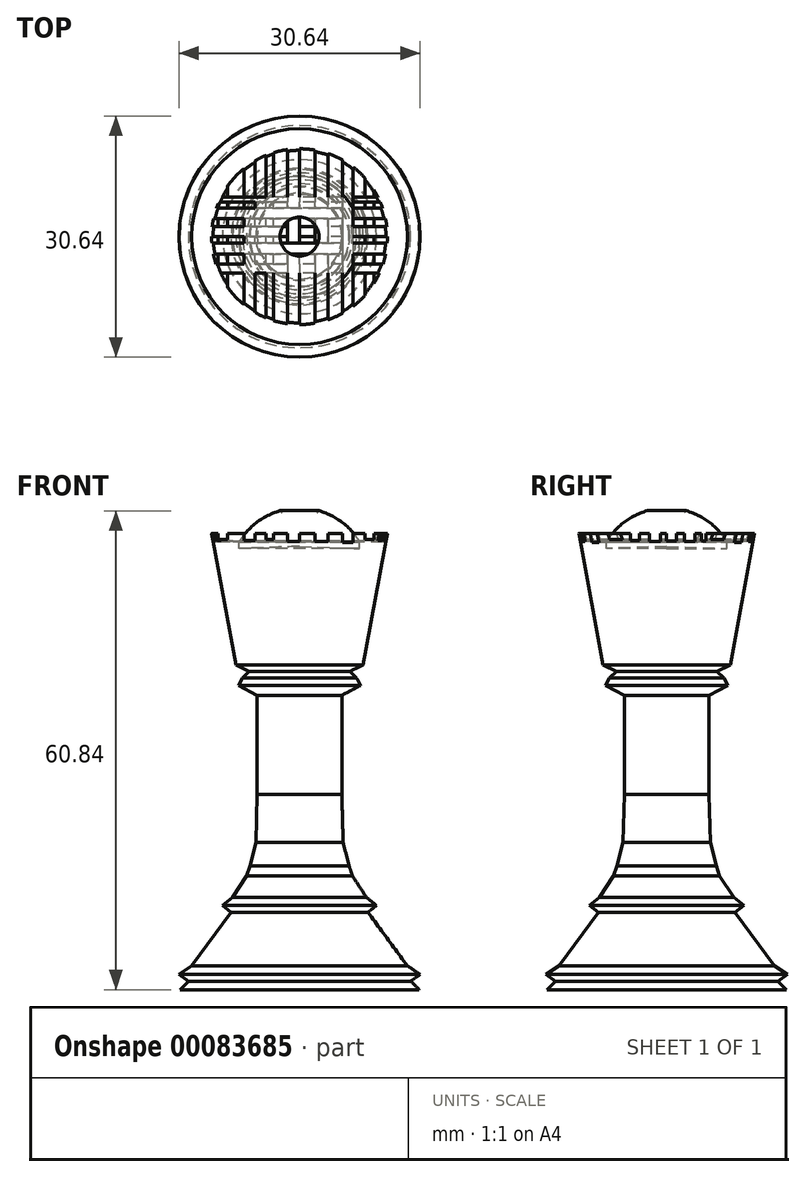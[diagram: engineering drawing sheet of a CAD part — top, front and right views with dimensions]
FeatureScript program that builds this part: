
annotation { "Feature Type Name" : "Feature", "Feature Type Description" : "" }
export const myFeature = defineFeature(function(context is Context, id is Id, definition is map)
    precondition{}
    {
        {
            var Q0;
            Q0=qCreatedBy(makeId("Front.planeOp"),FACE);
            var sketch = newSketch(context, id + "F0", { "sketchPlane" : qUnion([Q0])});
            skLineSegment(sketch, "E0", {"start": v(0, -41.24) * mm, "end": v(15.2, -41.24) * mm});
            skLineSegment(sketch, "E1", {"start": v(15.2, -41.24) * mm, "end": v(14.13, -40.16) * mm});
            skLineSegment(sketch, "E2", {"start": v(14.13, -40.16) * mm, "end": v(15.32, -39.3) * mm});
            skLineSegment(sketch, "E3", {"start": v(15.32, -39.3) * mm, "end": v(13.7, -38.2) * mm});
            skLineSegment(sketch, "E4", {"start": v(13.7, -38.2) * mm, "end": v(8.69, -31.4) * mm});
            skLineSegment(sketch, "E5", {"start": v(8.69, -31.4) * mm, "end": v(9.8, -30.55) * mm});
            skLineSegment(sketch, "E6", {"start": v(9.8, -30.55) * mm, "end": v(8.52, -29.53) * mm});
            skLineSegment(sketch, "E7", {"start": v(8.52, -29.53) * mm, "end": v(6.73, -26.81) * mm});
            skLineSegment(sketch, "E8", {"start": v(6.73, -26.81) * mm, "end": v(6.3, -25.54) * mm});
            skLineSegment(sketch, "E9", {"start": v(6.3, -25.54) * mm, "end": v(5.54, -22.56) * mm});
            skLineSegment(sketch, "E10", {"start": v(5.54, -22.56) * mm, "end": v(5.37, -16.44) * mm});
            skLineSegment(sketch, "E11", {"start": v(5.37, -16.44) * mm, "end": v(5.37, -3.86) * mm});
            skLineSegment(sketch, "E12", {"start": v(5.37, -3.86) * mm, "end": v(7.75, -2.58) * mm});
            skLineSegment(sketch, "E13", {"start": v(7.75, -2.58) * mm, "end": v(7.24, -1.64) * mm});
            skLineSegment(sketch, "E14", {"start": v(7.24, -1.64) * mm, "end": v(6.4, -0.8) * mm});
            skLineSegment(sketch, "E15", {"start": v(6.4, -0.8) * mm, "end": v(8.1, 0) * mm});
            skLineSegment(sketch, "E16", {"start": v(8.1, 0) * mm, "end": v(11.16, 16.74) * mm});
            skLineSegment(sketch, "E17", {"start": v(11.16, 16.74) * mm, "end": v(0, 16.74) * mm});
            skLineSegment(sketch, "E18", {"start": v(0, 16.74) * mm, "end": v(0, -41.24) * mm});
            skSolve(sketch);
        }
        {
            var Q0;
            Q0=makeQuery(id+"F0.imprint","IMPRINT",FACE,{"disambiguationData":[TD([[makeQuery(id+"F0.imprint","IMPRINT",EDGE,{"derivedFrom":sQuery(id+"F0.wireOp",EDGE,"E0")}),1.0]])]});
            var Q1;
            Q1=sQuery(id+"F0.wireOp",EDGE,"E18");
            revolve(context, id + "F1", {"entities" : qUnion([Q0]), "axis" : qUnion([Q1]), "revolveType" : RevolveType.FULL});
        }
        {
            var Q0;
            Q0=qCreatedBy(makeId("Front.planeOp"),FACE);
            var sketch = newSketch(context, id + "F2", { "sketchPlane" : qUnion([Q0])});
            skLineSegment(sketch, "E19.bottom", {"start": v(-1.55, 16.99) * mm, "end": v(0, 16.99) * mm});
            skLineSegment(sketch, "E19.top", {"start": v(-1.55, 15.7) * mm, "end": v(0, 15.7) * mm});
            skLineSegment(sketch, "E19.left", {"start": v(-1.55, 16.99) * mm, "end": v(-1.55, 15.7) * mm});
            skLineSegment(sketch, "E19.right", {"start": v(0, 16.99) * mm, "end": v(0, 15.7) * mm});
            skLineSegment(sketch, "E20.bottom", {"start": v(1.97, 16.87) * mm, "end": v(3.61, 16.87) * mm});
            skLineSegment(sketch, "E20.top", {"start": v(1.97, 15.7) * mm, "end": v(3.61, 15.7) * mm});
            skLineSegment(sketch, "E20.left", {"start": v(1.97, 16.87) * mm, "end": v(1.97, 15.7) * mm});
            skLineSegment(sketch, "E20.right", {"start": v(3.61, 16.87) * mm, "end": v(3.61, 15.7) * mm});
            skLineSegment(sketch, "E21.bottom", {"start": v(-7.06, 17.22) * mm, "end": v(-5.65, 17.22) * mm});
            skLineSegment(sketch, "E21.top", {"start": v(-7.06, 15.82) * mm, "end": v(-5.65, 15.82) * mm});
            skLineSegment(sketch, "E21.left", {"start": v(-7.06, 17.22) * mm, "end": v(-7.06, 15.82) * mm});
            skLineSegment(sketch, "E21.right", {"start": v(-5.65, 17.22) * mm, "end": v(-5.65, 15.82) * mm});
            skLineSegment(sketch, "E22.bottom", {"start": v(-4.24, 16.99) * mm, "end": v(-3.3, 16.99) * mm});
            skLineSegment(sketch, "E22.top", {"start": v(-4.24, 15.93) * mm, "end": v(-3.3, 15.93) * mm});
            skLineSegment(sketch, "E22.left", {"start": v(-4.24, 16.99) * mm, "end": v(-4.24, 15.93) * mm});
            skLineSegment(sketch, "E22.right", {"start": v(-3.3, 16.99) * mm, "end": v(-3.3, 15.93) * mm});
            skLineSegment(sketch, "E23.bottom", {"start": v(5.49, 16.87) * mm, "end": v(6.78, 16.87) * mm});
            skLineSegment(sketch, "E23.top", {"start": v(5.49, 15.58) * mm, "end": v(6.78, 15.58) * mm});
            skLineSegment(sketch, "E23.left", {"start": v(5.49, 16.87) * mm, "end": v(5.49, 15.58) * mm});
            skLineSegment(sketch, "E23.right", {"start": v(6.78, 16.87) * mm, "end": v(6.78, 15.58) * mm});
            skLineSegment(sketch, "E24.bottom", {"start": v(-10.34, 16.87) * mm, "end": v(-9.17, 16.87) * mm});
            skLineSegment(sketch, "E24.top", {"start": v(-10.34, 15.93) * mm, "end": v(-9.17, 15.93) * mm});
            skLineSegment(sketch, "E24.left", {"start": v(-10.34, 16.87) * mm, "end": v(-10.34, 15.93) * mm});
            skLineSegment(sketch, "E24.right", {"start": v(-9.17, 16.87) * mm, "end": v(-9.17, 15.93) * mm});
            skLineSegment(sketch, "E25.bottom", {"start": v(8.3, 17.1) * mm, "end": v(9.48, 17.1) * mm});
            skLineSegment(sketch, "E25.top", {"start": v(8.3, 15.93) * mm, "end": v(9.48, 15.93) * mm});
            skLineSegment(sketch, "E25.left", {"start": v(8.3, 17.1) * mm, "end": v(8.3, 15.93) * mm});
            skLineSegment(sketch, "E25.right", {"start": v(9.48, 17.1) * mm, "end": v(9.48, 15.93) * mm});
            skSolve(sketch);
        }
        {
            var Q0;
            Q0 = qSketchRegion(id + "F2", true);
            var Q1;
            Q1 = qConstructionFilter(qBodyType(qCreatedBy(id + "F2" ,EDGE), BodyType.WIRE), ConstructionObject.NO);
            extrude(context, id + "F3", {"entities" : qUnion([Q0]), "operationType" : NewBodyOperationType.REMOVE, "surfaceEntities" : qUnion([Q1]), "oppositeDirection" : true, "depth" : 25 * mm, "hasSecondDirection" : true, "secondDirectionOppositeDirection" : false, "secondDirectionDepth" : 25 * mm});
        }
        {
            var Q0;
            Q0=qCreatedBy(makeId("Right.planeOp"),FACE);
            var sketch = newSketch(context, id + "F4", { "sketchPlane" : qUnion([Q0])});
            skLineSegment(sketch, "E26.bottom", {"start": v(-4.63, 16.84) * mm, "end": v(-3.45, 16.84) * mm});
            skLineSegment(sketch, "E26.top", {"start": v(-4.63, 15.81) * mm, "end": v(-3.45, 15.81) * mm});
            skLineSegment(sketch, "E26.left", {"start": v(-4.63, 16.84) * mm, "end": v(-4.63, 15.81) * mm});
            skLineSegment(sketch, "E26.right", {"start": v(-3.45, 16.84) * mm, "end": v(-3.45, 15.81) * mm});
            skLineSegment(sketch, "E27.bottom", {"start": v(-2.2, 16.92) * mm, "end": v(-0.8, 16.92) * mm});
            skLineSegment(sketch, "E27.top", {"start": v(-2.2, 15.67) * mm, "end": v(-0.8, 15.67) * mm});
            skLineSegment(sketch, "E27.left", {"start": v(-2.2, 16.92) * mm, "end": v(-2.2, 15.67) * mm});
            skLineSegment(sketch, "E27.right", {"start": v(-0.8, 16.92) * mm, "end": v(-0.8, 15.67) * mm});
            skLineSegment(sketch, "E28.bottom", {"start": v(0, 16.84) * mm, "end": v(1.26, 16.84) * mm});
            skLineSegment(sketch, "E28.top", {"start": v(0, 15.74) * mm, "end": v(1.26, 15.74) * mm});
            skLineSegment(sketch, "E28.left", {"start": v(0, 16.84) * mm, "end": v(0, 15.74) * mm});
            skLineSegment(sketch, "E28.right", {"start": v(1.26, 16.84) * mm, "end": v(1.26, 15.74) * mm});
            skLineSegment(sketch, "E29.bottom", {"start": v(2.29, 16.77) * mm, "end": v(3.61, 16.77) * mm});
            skLineSegment(sketch, "E29.top", {"start": v(2.29, 15.67) * mm, "end": v(3.61, 15.67) * mm});
            skLineSegment(sketch, "E29.left", {"start": v(2.29, 16.77) * mm, "end": v(2.29, 15.67) * mm});
            skLineSegment(sketch, "E29.right", {"start": v(3.61, 16.77) * mm, "end": v(3.61, 15.67) * mm});
            skLineSegment(sketch, "E30.bottom", {"start": v(4.42, 16.77) * mm, "end": v(5, 16.77) * mm});
            skLineSegment(sketch, "E30.top", {"start": v(4.42, 15.74) * mm, "end": v(5, 15.74) * mm});
            skLineSegment(sketch, "E30.left", {"start": v(4.42, 16.77) * mm, "end": v(4.42, 15.74) * mm});
            skLineSegment(sketch, "E30.right", {"start": v(5, 16.77) * mm, "end": v(5, 15.74) * mm});
            skSolve(sketch);
        }
        {
            var Q0;
            Q0 = qSketchRegion(id + "F4", true);
            var Q1;
            Q1=sQuery(id+"F4.wireOp",EDGE,"E27.bottom");
            extrude(context, id + "F5", {"entities" : qUnion([Q0]), "operationType" : NewBodyOperationType.REMOVE, "surfaceEntities" : qUnion([Q1]), "oppositeDirection" : true, "depth" : 25 * mm, "hasSecondDirection" : true, "secondDirectionOppositeDirection" : false, "secondDirectionDepth" : 25 * mm});
        }
        {
            var Q0;
            Q0=qCreatedBy(makeId("Front.planeOp"),FACE);
            var sketch = newSketch(context, id + "F6", { "sketchPlane" : qUnion([Q0])});
            skArc(sketch, "E31", {"start": v(7.65, 15.64) * mm, "mid": v(-0.06, 19.93) * mm, "end": v(-7.6, 15.35) * mm});
            skLineSegment(sketch, "E32", {"start": v(7.65, 15.64) * mm, "end": v(7.65, 14.78) * mm});
            skLineSegment(sketch, "E33", {"start": v(7.65, 14.78) * mm, "end": v(-7.6, 15.35) * mm});
            skLineSegment(sketch, "E34", {"start": v(0, 19.93) * mm, "end": v(0, 15.07) * mm});
            skSolve(sketch);
        }
        {
            var Q0;
            {var subQ0=sQuery(id+"F6.wireOp",EDGE,"E32");Q0=makeQuery(id+"F6.imprint","IMPRINT",FACE,{"disambiguationData":[TD([[makeQuery(id+"F6.imprint","IMPRINT",EDGE,{"derivedFrom":subQ0}),-1.0]])]});}
            var Q1;
            Q1=sQuery(id+"F6.wireOp",EDGE,"E34");
            revolve(context, id + "F7", {"entities" : qUnion([Q0]), "axis" : qUnion([Q1]), "revolveType" : RevolveType.FULL});
        }
        {
            var Q0;
            Q0=qCreatedBy(makeId("Front.planeOp"),FACE);
            var sketch = newSketch(context, id + "F8", { "sketchPlane" : qUnion([Q0])});
            skLineSegment(sketch, "E35", {"start": v(0, 21.98) * mm, "end": v(0, 18.11) * mm});
            skArc(sketch, "E36", {"start": v(2.1, 19.25) * mm, "mid": v(2.48, 21.72) * mm, "end": v(0, 21.98) * mm});
            skLineSegment(sketch, "E37", {"start": v(0, 18.11) * mm, "end": v(2.1, 19.25) * mm});
            skSolve(sketch);
        }
        {
            var Q0;
            Q0 = qSketchRegion(id + "F8", true);
            var Q1;
            Q1=sQuery(id+"F8.wireOp",EDGE,"E35");
            var Q2;
            Q2=sQuery(id+"F8.wireOp",EDGE,"E35");
            revolve(context, id + "F9", {"operationType" : NewBodyOperationType.ADD, "entities" : qUnion([Q0]), "axis" : qUnion([Q1, Q2]), "revolveType" : RevolveType.FULL});
        }
    });
